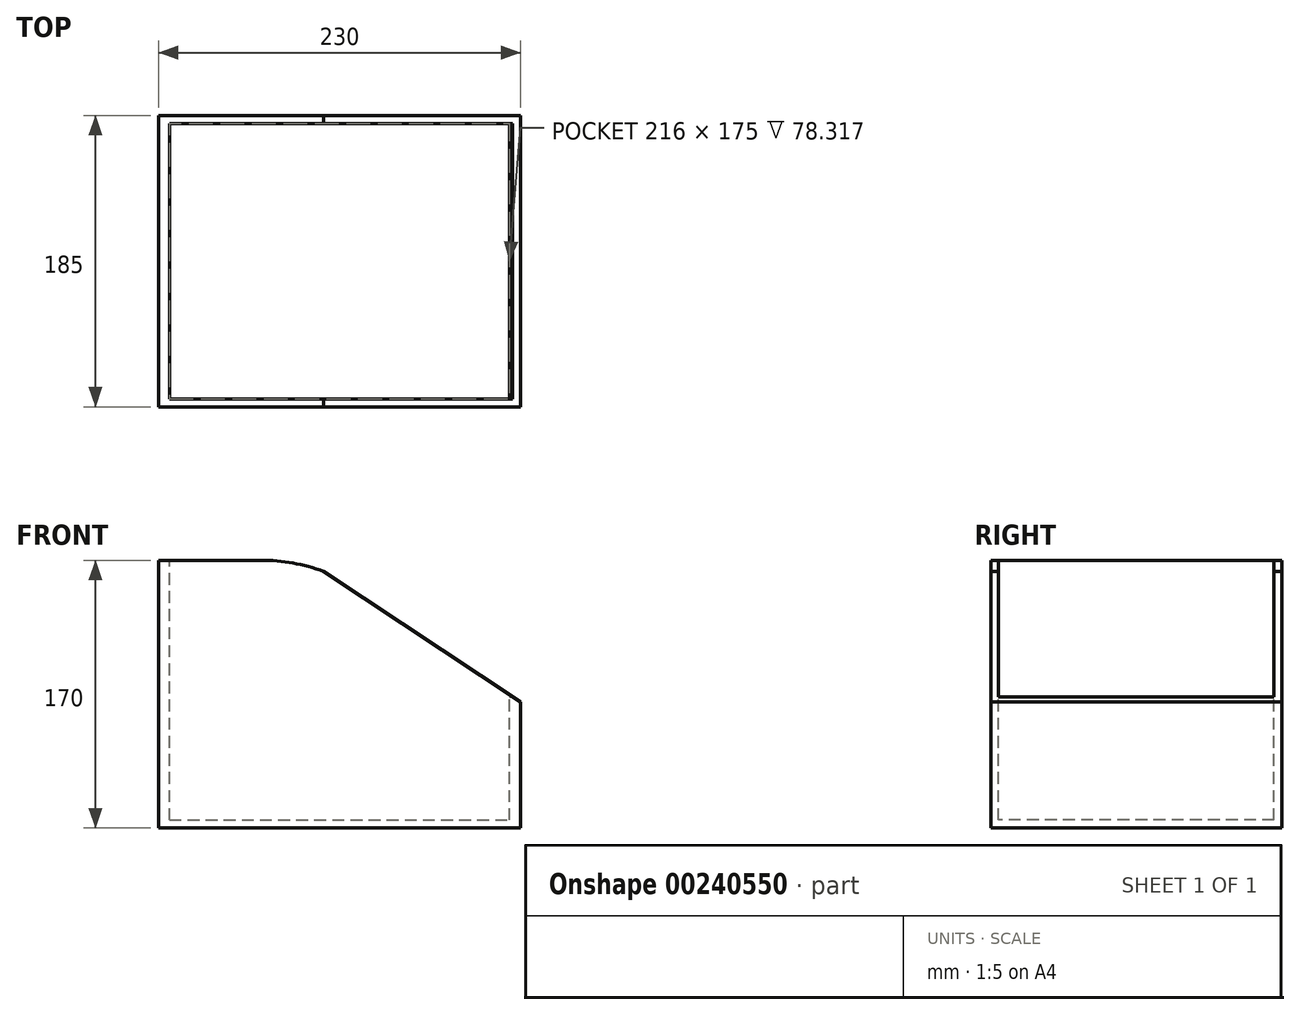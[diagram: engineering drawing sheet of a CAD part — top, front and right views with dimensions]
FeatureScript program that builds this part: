
annotation { "Feature Type Name" : "Feature", "Feature Type Description" : "" }
export const myFeature = defineFeature(function(context is Context, id is Id, definition is map)
    precondition{}
    {
        {
            var Q0;
            Q0=qCreatedBy(makeId("Front.planeOp"),FACE);
            var sketch = newSketch(context, id + "F0", { "sketchPlane" : qUnion([Q0])});
            skLineSegment(sketch, "E0", {"start": v(-105, 141.4) * mm, "end": v(-105, -28.6) * mm});
            skLineSegment(sketch, "E1", {"start": v(-105, -28.6) * mm, "end": v(125, -28.6) * mm});
            skLineSegment(sketch, "E2", {"start": v(125, -28.6) * mm, "end": v(125, 51.4) * mm});
            skLineSegment(sketch, "E3", {"start": v(125, 51.4) * mm, "end": v(0, 134.31) * mm});
            skLineSegment(sketch, "E4", {"start": v(-105, 141.4) * mm, "end": v(-39.85, 141.4) * mm});
            skLineSegment(sketch, "E5", {"start": v(125, 51.4) * mm, "end": v(0, 51.73) * mm});
            skArc(sketch, "E6", {"start": v(-39.85, 141.4) * mm, "mid": v(-19.61, 139.61) * mm, "end": v(0, 134.31) * mm});
            skSolve(sketch);
        }
        {
            var Q0;
            Q0=makeQuery(id+"F0.imprint","IMPRINT",FACE,{"disambiguationData":[TD([[makeQuery(id+"F0.imprint","IMPRINT",EDGE,{"derivedFrom":sQuery(id+"F0.wireOp",EDGE,"E0")}),1.0]])]});
            extrude(context, id + "F1", {"entities" : qUnion([Q0]), "endBound" : BoundingType.SYMMETRIC, "depth" : 185 * mm});
        }
        {
            var Q0;
            Q0=makeQuery(id+"F1.opExtrude","SWEPT_FACE",FACE,{"disambiguationData":[OSD([sQuery(id+"F0.wireOp",EDGE,"E1")])]});
            var sketch = newSketch(context, id + "F2", { "sketchPlane" : qUnion([Q0])});
            skLineSegment(sketch, "E7.0", {"start": v(-100, -87.5) * mm, "end": v(120, -87.5) * mm});
            skLineSegment(sketch, "E7.1", {"start": v(-100, 87.5) * mm, "end": v(-100, -87.5) * mm});
            skLineSegment(sketch, "E7.2", {"start": v(120, 87.5) * mm, "end": v(-100, 87.5) * mm});
            skLineSegment(sketch, "E7.3", {"start": v(120, -87.5) * mm, "end": v(120, 87.5) * mm});
            skSolve(sketch);
        }
        {
            var Q0;
            Q0=qSketchRegion(id+"F2",true);
            extrude(context, id + "F3", {"entities" : qUnion([Q0]), "operationType" : NewBodyOperationType.ADD, "oppositeDirection" : true, "depth" : 200 * mm});
        }
        {
            var Q0;
            Q0=makeQuery(id+"F3.opExtrude","CAP_FACE",FACE,{"disambiguationData":[OSD([sQuery(id+"F2.wireOp",EDGE,"E7.0"),sQuery(id+"F2.wireOp",EDGE,"E7.1"),sQuery(id+"F2.wireOp",EDGE,"E7.2"),sQuery(id+"F2.wireOp",EDGE,"E7.3")])],"isStart":false});
            extrude(context, id + "F4", {"entities" : qUnion([Q0]), "operationType" : NewBodyOperationType.REMOVE, "oppositeDirection" : true, "depth" : 195 * mm});
        }
        {
            var Q0;
            Q0=makeQuery(id+"F4.boolean.opBoolean","COPY",FACE,{"derivedFrom":makeQuery(id+"F4.opExtrude","SWEPT_FACE",FACE,{"disambiguationData":[OSD([sQuery(id+"F2.wireOp",EDGE,"E7.1")])]})});
            extrude(context, id + "F5", {"entities" : qUnion([Q0]), "operationType" : NewBodyOperationType.ADD, "depth" : 2 * mm});
        }
        {
            var Q0;
            Q0=makeQuery(id+"F4.boolean.opBoolean","COPY",FACE,{"derivedFrom":makeQuery(id+"F4.opExtrude","SWEPT_FACE",FACE,{"disambiguationData":[OSD([sQuery(id+"F2.wireOp",EDGE,"E7.3")])]})});
            extrude(context, id + "F6", {"entities" : qUnion([Q0]), "operationType" : NewBodyOperationType.ADD, "depth" : 2 * mm});
        }
    });
